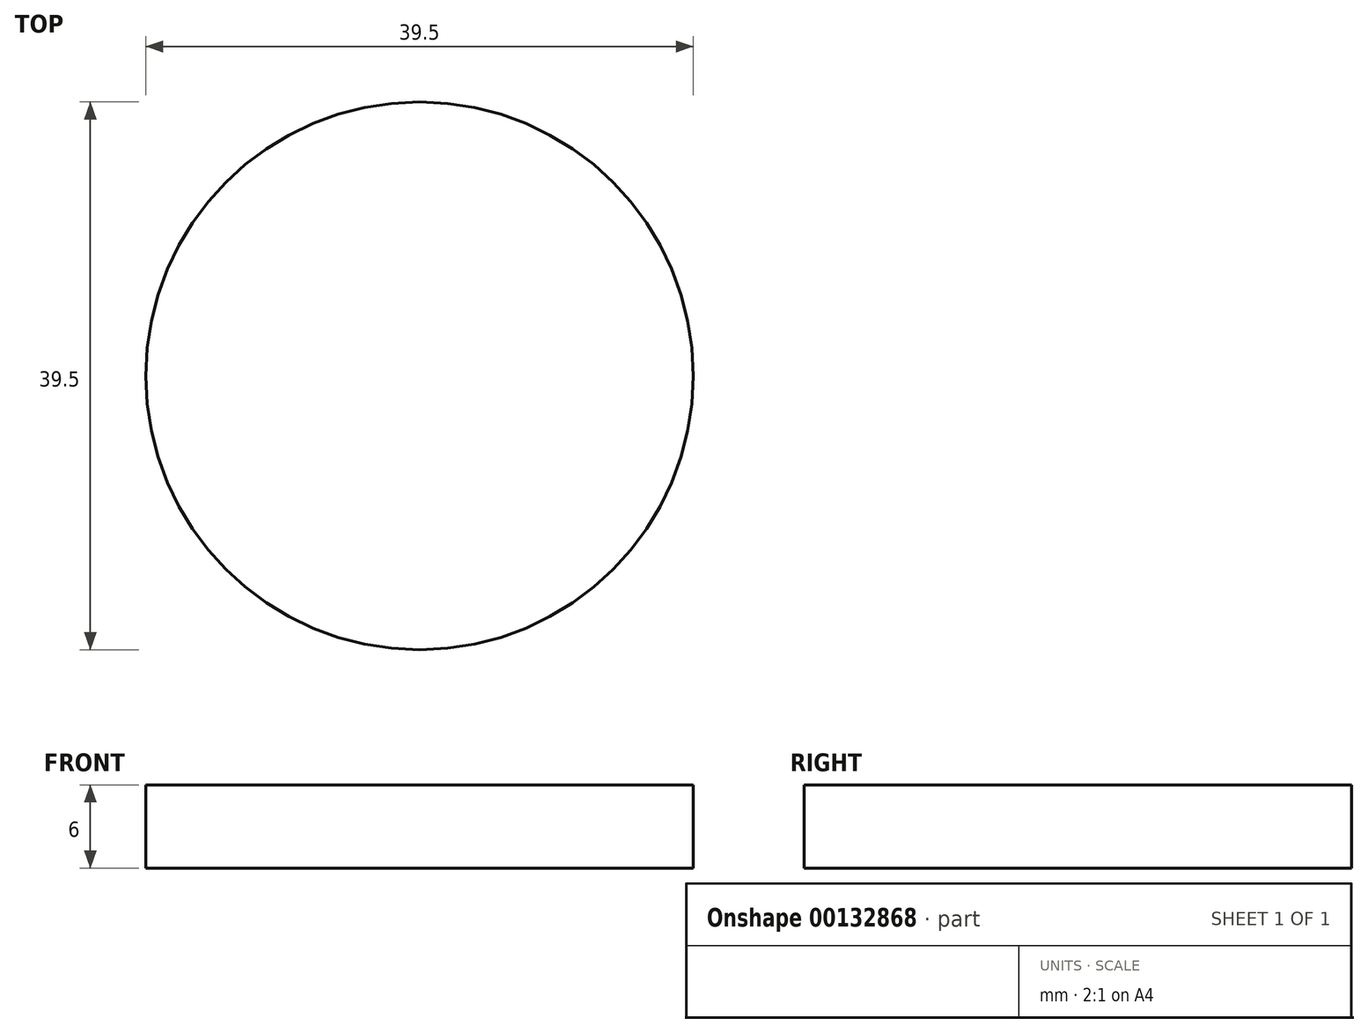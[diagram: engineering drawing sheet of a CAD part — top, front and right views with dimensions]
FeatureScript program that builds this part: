
annotation { "Feature Type Name" : "Feature", "Feature Type Description" : "" }
export const myFeature = defineFeature(function(context is Context, id is Id, definition is map)
    precondition{}
    {
        {
            var Q0;
            Q0=qCreatedBy(makeId("Top.planeOp"),FACE);
            var sketch = newSketch(context, id + "F0", { "sketchPlane" : qUnion([Q0])});
            skCircle(sketch, "E0", {"center": v(0, 0) * mm, "radius": 19.75 * mm});
            skSolve(sketch);
        }
        {
            var Q0;
            Q0 = qSketchRegion(id + "F0", true);
            extrude(context, id + "F1", {"entities" : qUnion([Q0]), "depth" : 6 * mm});
        }
    });
